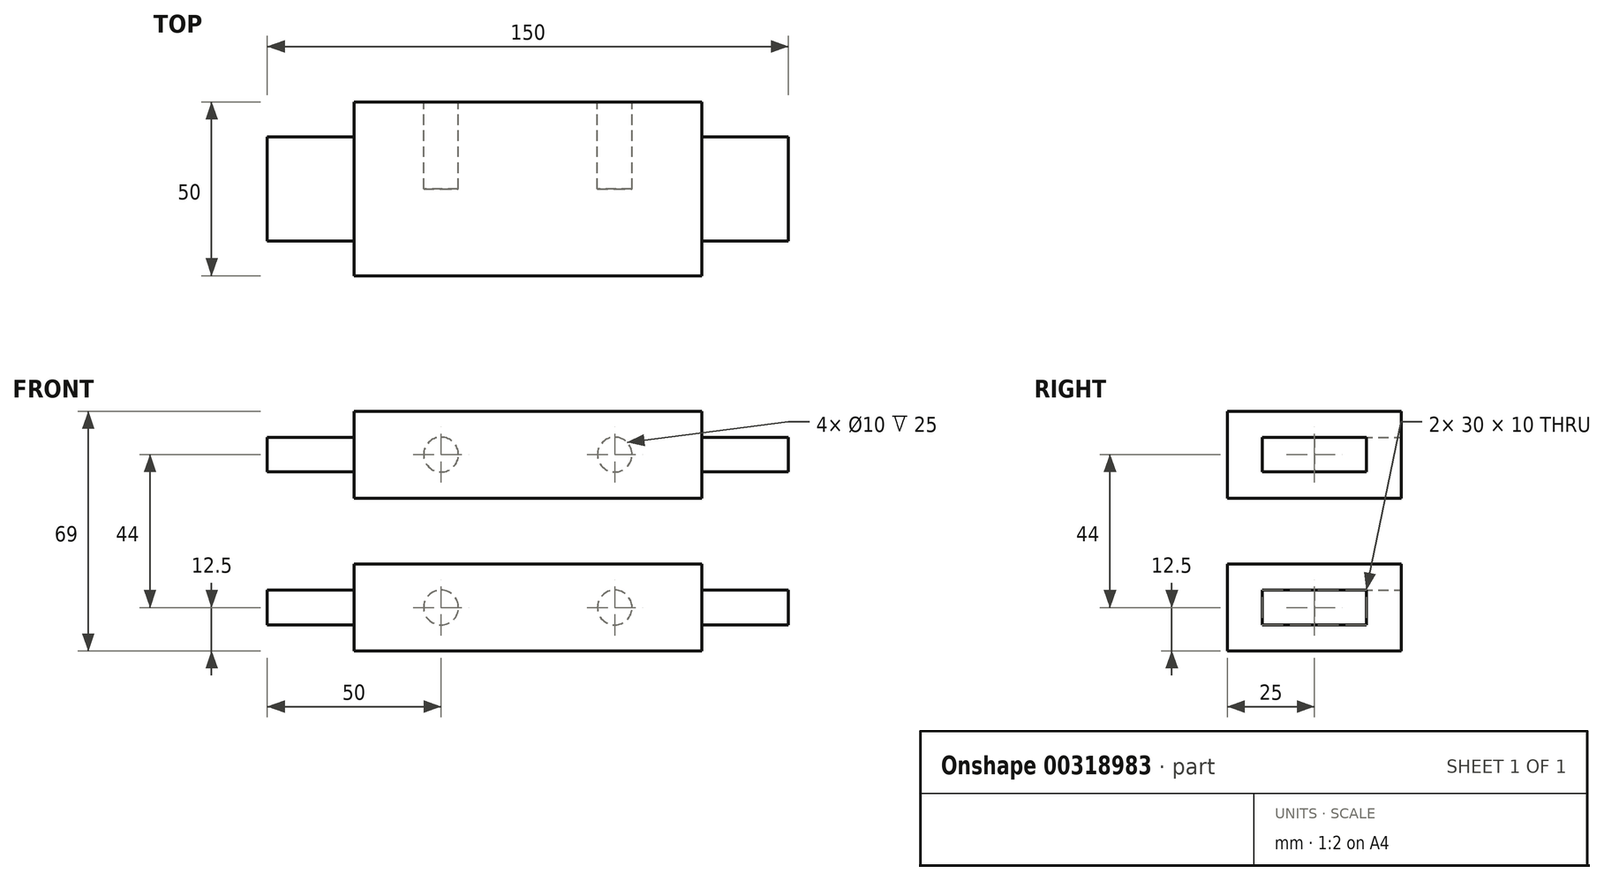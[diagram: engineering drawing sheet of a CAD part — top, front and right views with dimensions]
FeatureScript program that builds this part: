
annotation { "Feature Type Name" : "Feature", "Feature Type Description" : "" }
export const myFeature = defineFeature(function(context is Context, id is Id, definition is map)
    precondition{}
    {
        {
            var Q0;
            Q0=qCreatedBy(makeId("Top.planeOp"),FACE);
            var sketch = newSketch(context, id + "F0", { "sketchPlane" : qUnion([Q0])});
            skLineSegment(sketch, "E0.bottom", {"start": v(50, 25) * mm, "end": v(-50, 25) * mm});
            skLineSegment(sketch, "E0.top", {"start": v(50, -25) * mm, "end": v(-50, -25) * mm});
            skLineSegment(sketch, "E0.left", {"start": v(50, 25) * mm, "end": v(50, -25) * mm});
            skLineSegment(sketch, "E0.right", {"start": v(-50, 25) * mm, "end": v(-50, -25) * mm});
            skPoint(sketch, "E0.middle", {"position": v(0, 0) * mm});
            skSolve(sketch);
        }
        {
            var Q0;
            Q0 = qSketchRegion(id + "F0", true);
            extrude(context, id + "F1", {"entities" : qUnion([Q0]), "depth" : 25 * mm});
        }
        {
            var Q0;
            Q0=makeQuery(id+"F1.opExtrude","SWEPT_FACE",FACE,{"disambiguationData":[OSD([sQuery(id+"F0.wireOp",EDGE,"E0.right")])]});
            var sketch = newSketch(context, id + "F2", { "sketchPlane" : qUnion([Q0])});
            skLineSegment(sketch, "E1", {"start": v(-15, 25) * mm, "end": v(-15, 17.5) * mm, "construction": true});
            skLineSegment(sketch, "E2", {"start": v(-15, 17.5) * mm, "end": v(-25, 17.5) * mm, "construction": true});
            skLineSegment(sketch, "E3.bottom", {"start": v(-15, 17.5) * mm, "end": v(15, 17.5) * mm});
            skLineSegment(sketch, "E3.top", {"start": v(-15, 7.5) * mm, "end": v(15, 7.5) * mm});
            skLineSegment(sketch, "E3.left", {"start": v(-15, 17.5) * mm, "end": v(-15, 7.5) * mm});
            skLineSegment(sketch, "E3.right", {"start": v(15, 17.5) * mm, "end": v(15, 7.5) * mm});
            skSolve(sketch);
        }
        {
            var Q0;
            Q0 = qSketchRegion(id + "F2", true);
            extrude(context, id + "F3", {"entities" : qUnion([Q0]), "operationType" : NewBodyOperationType.ADD, "depth" : 25 * mm});
        }
        {
            var Q0;
            Q0=makeQuery(id+"F1.opExtrude","SWEPT_BODY",BODY,{"disambiguationData":[OSD([sQuery(id+"F0.wireOp",EDGE,"E0.bottom"),sQuery(id+"F0.wireOp",EDGE,"E0.top"),sQuery(id+"F0.wireOp",EDGE,"E0.left"),sQuery(id+"F0.wireOp",EDGE,"E0.right")])]});
            var Q1;
            Q1=qCreatedBy(makeId("Right.planeOp"),FACE);
            mirror(context, id + "F4", {"operationType" : NewBodyOperationType.ADD, "entities" : qUnion([Q0]), "mirrorPlane" : qUnion([Q1])});
        }
        {
            var Q0;
            Q0=makeQuery(id+"F1.opExtrude","SWEPT_FACE",FACE,{"disambiguationData":[OSD([sQuery(id+"F0.wireOp",EDGE,"E0.bottom")])]});
            var sketch = newSketch(context, id + "F5", { "sketchPlane" : qUnion([Q0])});
            skLineSegment(sketch, "E4", {"start": v(50, 12.5) * mm, "end": v(-50, 12.5) * mm, "construction": true});
            skPoint(sketch, "E5", {"position": v(25, 12.5) * mm});
            skCircle(sketch, "E6", {"center": v(25, 12.5) * mm, "radius": 5 * mm});
            skPoint(sketch, "E7", {"position": v(-25, 12.5) * mm});
            skCircle(sketch, "E8", {"center": v(-25, 12.5) * mm, "radius": 5 * mm});
            skSolve(sketch);
        }
        {
            var Q0;
            Q0=makeQuery(id+"F5.imprint","IMPRINT",FACE,{"disambiguationData":[TD([[makeQuery(id+"F5.imprint","IMPRINT",EDGE,{"derivedFrom":sQuery(id+"F5.wireOp",EDGE,"E6")}),1.0]])]});
            var Q1;
            Q1=makeQuery(id+"F5.imprint","IMPRINT",FACE,{"disambiguationData":[TD([[makeQuery(id+"F5.imprint","IMPRINT",EDGE,{"derivedFrom":sQuery(id+"F5.wireOp",EDGE,"E8")}),1.0]])]});
            extrude(context, id + "F6", {"entities" : qUnion([Q0, Q1]), "operationType" : NewBodyOperationType.REMOVE, "oppositeDirection" : true, "depth" : 25 * mm});
        }
        {
            var Q0;
            Q0=makeQuery(id+"F1.opExtrude","SWEPT_BODY",BODY,{"disambiguationData":[OSD([sQuery(id+"F0.wireOp",EDGE,"E0.bottom"),sQuery(id+"F0.wireOp",EDGE,"E0.top"),sQuery(id+"F0.wireOp",EDGE,"E0.left"),sQuery(id+"F0.wireOp",EDGE,"E0.right")])]});
            transform(context, id + "F7", {"entities" : qUnion([Q0]), "transformType" : TransformType.TRANSLATION_3D, "dx" : 0 * mm, "dy" : 0 * mm, "dz" : 44 * mm, "makeCopy" : true});
        }
    });
